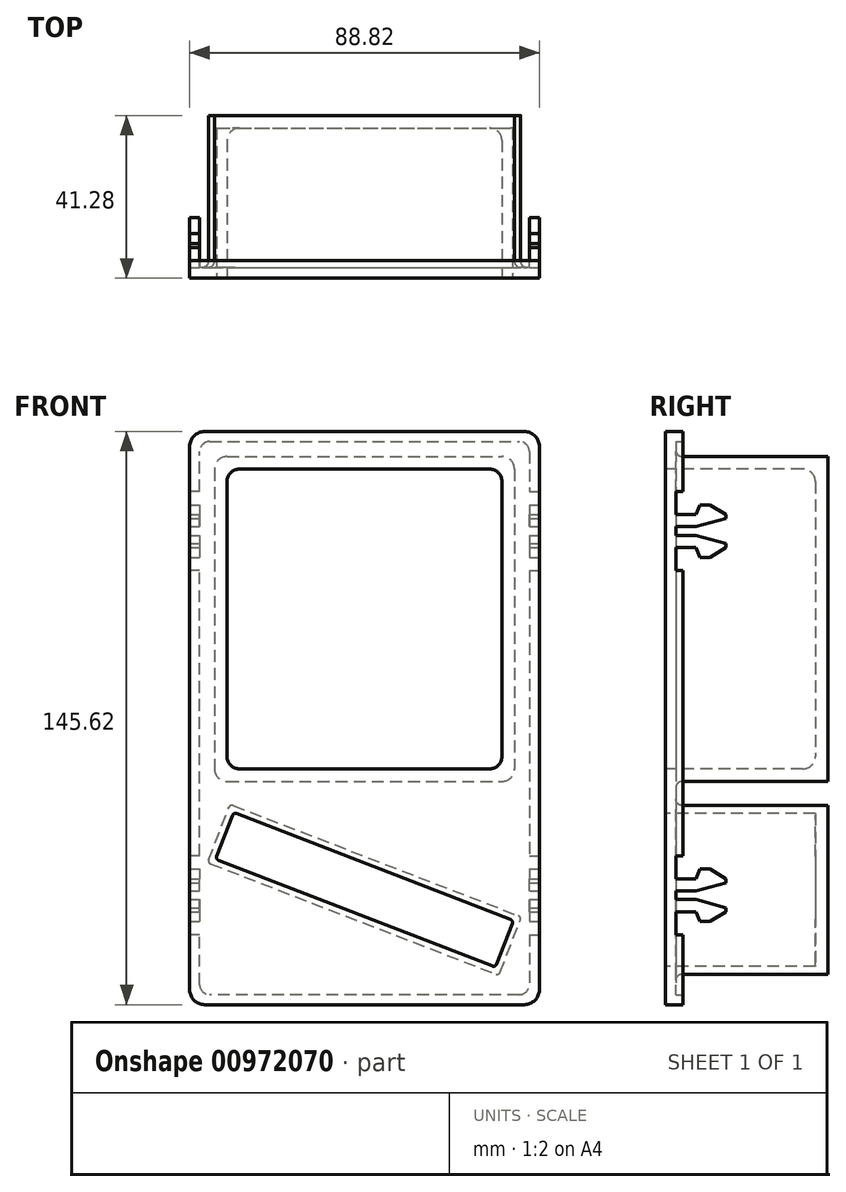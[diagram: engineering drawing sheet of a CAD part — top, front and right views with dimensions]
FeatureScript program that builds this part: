
annotation { "Feature Type Name" : "Feature", "Feature Type Description" : "" }
export const myFeature = defineFeature(function(context is Context, id is Id, definition is map)
    precondition{}
    {
        {
            var Q0;
            Q0=qCreatedBy(makeId("Front.planeOp"),FACE);
            var sketch = newSketch(context, id + "F0", { "sketchPlane" : qUnion([Q0])});
            skLineSegment(sketch, "E0.bottom", {"start": v(-40.6, 72.8) * mm, "end": v(40.6, 72.8) * mm});
            skLineSegment(sketch, "E0.top", {"start": v(-40.6, -72.8) * mm, "end": v(40.6, -72.8) * mm});
            skLineSegment(sketch, "E0.left", {"start": v(-44.41, 69) * mm, "end": v(-44.41, -69) * mm});
            skLineSegment(sketch, "E0.right", {"start": v(44.41, 69) * mm, "end": v(44.41, -69) * mm});
            skPoint(sketch, "E0.middle", {"position": v(0, 0) * mm});
            skPoint(sketch, "E1.visualSharp", {"position": v(-44.41, -72.8) * mm});
            skArc(sketch, "E1.filletArc", {"start": v(-44.41, -69) * mm, "mid": v(-43.3, -71.7) * mm, "end": v(-40.6, -72.8) * mm});
            skPoint(sketch, "E2.visualSharp", {"position": v(44.41, -72.8) * mm});
            skArc(sketch, "E2.filletArc", {"start": v(40.6, -72.8) * mm, "mid": v(43.3, -71.7) * mm, "end": v(44.41, -69) * mm});
            skPoint(sketch, "E3.visualSharp", {"position": v(44.41, 72.8) * mm});
            skArc(sketch, "E3.filletArc", {"start": v(44.41, 69) * mm, "mid": v(43.3, 71.7) * mm, "end": v(40.6, 72.8) * mm});
            skPoint(sketch, "E4.visualSharp", {"position": v(-44.41, 72.8) * mm});
            skArc(sketch, "E4.filletArc", {"start": v(-40.6, 72.8) * mm, "mid": v(-43.3, 71.7) * mm, "end": v(-44.41, 69) * mm});
            skSolve(sketch);
        }
        {
            var Q0;
            Q0=makeQuery(id+"F0.imprint","IMPRINT",FACE,{"disambiguationData":[TD([[makeQuery(id+"F0.imprint","IMPRINT",EDGE,{"derivedFrom":sQuery(id+"F0.wireOp",EDGE,"E0.bottom")}),-1.0]])]});
            extrude(context, id + "F1", {"entities" : qUnion([Q0]), "depth" : 4.44 * mm, "offsetDistance" : 25.4 * mm});
        }
        {
            var Q0;
            Q0=makeQuery(id+"F0.imprint","IMPRINT",FACE,{"disambiguationData":[TD([[makeQuery(id+"F0.imprint","IMPRINT",EDGE,{"derivedFrom":sQuery(id+"F0.wireOp",EDGE,"E0.bottom")}),-1.0]])]});
            var sketch = newSketch(context, id + "F2", { "sketchPlane" : qUnion([Q0])});
            skLineSegment(sketch, "E5", {"start": v(41.87, 67.73) * mm, "end": v(41.87, -67.73) * mm});
            skLineSegment(sketch, "E6", {"start": v(39.33, -70.27) * mm, "end": v(-39.33, -70.27) * mm});
            skLineSegment(sketch, "E7", {"start": v(-41.87, -67.73) * mm, "end": v(-41.87, 67.73) * mm});
            skLineSegment(sketch, "E8", {"start": v(-39.33, 70.27) * mm, "end": v(39.33, 70.27) * mm});
            skPoint(sketch, "E9.visualSharp", {"position": v(41.87, 70.27) * mm});
            skArc(sketch, "E9.filletArc", {"start": v(41.87, 67.73) * mm, "mid": v(41.13, 69.53) * mm, "end": v(39.33, 70.27) * mm});
            skPoint(sketch, "E10.visualSharp", {"position": v(-41.87, 70.27) * mm});
            skArc(sketch, "E10.filletArc", {"start": v(-39.33, 70.27) * mm, "mid": v(-41.13, 69.53) * mm, "end": v(-41.87, 67.73) * mm});
            skPoint(sketch, "E11.visualSharp", {"position": v(-41.87, -70.27) * mm});
            skArc(sketch, "E11.filletArc", {"start": v(-41.87, -67.73) * mm, "mid": v(-41.13, -69.53) * mm, "end": v(-39.33, -70.27) * mm});
            skPoint(sketch, "E12.visualSharp", {"position": v(41.87, -70.27) * mm});
            skArc(sketch, "E12.filletArc", {"start": v(39.33, -70.27) * mm, "mid": v(41.13, -69.53) * mm, "end": v(41.87, -67.73) * mm});
            skSolve(sketch);
        }
        {
            var Q0;
            Q0=qSketchRegion(id+"F2",true);
            extrude(context, id + "F3", {"entities" : qUnion([Q0]), "operationType" : NewBodyOperationType.REMOVE, "depth" : 1.78 * mm, "offsetDistance" : 25.4 * mm});
        }
        {
            var Q0;
            Q0=makeQuery(id+"F1.opExtrude","CAP_FACE",FACE,{"disambiguationData":[OSD([sQuery(id+"F0.wireOp",EDGE,"E0.bottom"),sQuery(id+"F0.wireOp",EDGE,"E0.top"),sQuery(id+"F0.wireOp",EDGE,"E0.left"),sQuery(id+"F0.wireOp",EDGE,"E0.right"),sQuery(id+"F0.wireOp",EDGE,"E1.filletArc"),sQuery(id+"F0.wireOp",EDGE,"E2.filletArc"),sQuery(id+"F0.wireOp",EDGE,"E3.filletArc"),sQuery(id+"F0.wireOp",EDGE,"E4.filletArc")])],"isStart":false});
            var sketch = newSketch(context, id + "F4", { "sketchPlane" : qUnion([Q0])});
            skLineSegment(sketch, "E13", {"start": v(-31.75, 63.28) * mm, "end": v(31.75, 63.28) * mm});
            skLineSegment(sketch, "E14", {"start": v(-34.93, 60.1) * mm, "end": v(-34.93, -9.74) * mm});
            skLineSegment(sketch, "E15", {"start": v(-31.75, -12.92) * mm, "end": v(31.75, -12.92) * mm});
            skLineSegment(sketch, "E16", {"start": v(34.93, -9.74) * mm, "end": v(34.93, 60.1) * mm});
            skPoint(sketch, "E17.visualSharp", {"position": v(-34.93, 63.28) * mm});
            skArc(sketch, "E17.filletArc", {"start": v(-31.75, 63.28) * mm, "mid": v(-34, 62.35) * mm, "end": v(-34.92, 60.1) * mm});
            skPoint(sketch, "E18.visualSharp", {"position": v(34.93, 63.28) * mm});
            skArc(sketch, "E18.filletArc", {"start": v(34.93, 60.1) * mm, "mid": v(34, 62.35) * mm, "end": v(31.75, 63.28) * mm});
            skPoint(sketch, "E19.visualSharp", {"position": v(-34.93, -12.92) * mm});
            skArc(sketch, "E19.filletArc", {"start": v(-34.93, -9.74) * mm, "mid": v(-34, -11.99) * mm, "end": v(-31.75, -12.92) * mm});
            skPoint(sketch, "E20.visualSharp", {"position": v(34.93, -12.92) * mm});
            skArc(sketch, "E20.filletArc", {"start": v(31.75, -12.92) * mm, "mid": v(34, -11.99) * mm, "end": v(34.93, -9.74) * mm});
            skSolve(sketch);
        }
        {
            var Q0;
            Q0=makeQuery(id+"F1.opExtrude","CAP_FACE",FACE,{"disambiguationData":[OSD([sQuery(id+"F0.wireOp",EDGE,"E0.bottom"),sQuery(id+"F0.wireOp",EDGE,"E0.top"),sQuery(id+"F0.wireOp",EDGE,"E0.left"),sQuery(id+"F0.wireOp",EDGE,"E0.right"),sQuery(id+"F0.wireOp",EDGE,"E1.filletArc"),sQuery(id+"F0.wireOp",EDGE,"E2.filletArc"),sQuery(id+"F0.wireOp",EDGE,"E3.filletArc"),sQuery(id+"F0.wireOp",EDGE,"E4.filletArc")])],"isStart":false});
            var sketch = newSketch(context, id + "F5", { "sketchPlane" : qUnion([Q0])});
            skLineSegment(sketch, "E21", {"start": v(-34.92, 66.46) * mm, "end": v(34.92, 66.46) * mm});
            skLineSegment(sketch, "E22", {"start": v(-38.1, 63.28) * mm, "end": v(-38.1, -12.92) * mm});
            skLineSegment(sketch, "E23", {"start": v(-34.92, -16.1) * mm, "end": v(34.93, -16.1) * mm});
            skLineSegment(sketch, "E24", {"start": v(38.1, 63.28) * mm, "end": v(38.1, -12.92) * mm});
            skPoint(sketch, "E25.visualSharp", {"position": v(-38.1, 66.46) * mm});
            skArc(sketch, "E25.filletArc", {"start": v(-34.92, 66.46) * mm, "mid": v(-37.17, 65.53) * mm, "end": v(-38.1, 63.28) * mm});
            skPoint(sketch, "E26.visualSharp", {"position": v(-38.1, -16.1) * mm});
            skArc(sketch, "E26.filletArc", {"start": v(-38.1, -12.92) * mm, "mid": v(-37.17, -15.16) * mm, "end": v(-34.92, -16.1) * mm});
            skPoint(sketch, "E27.visualSharp", {"position": v(38.1, -16.1) * mm});
            skArc(sketch, "E27.filletArc", {"start": v(34.93, -16.1) * mm, "mid": v(37.17, -15.16) * mm, "end": v(38.1, -12.92) * mm});
            skPoint(sketch, "E28.visualSharp", {"position": v(38.1, 66.46) * mm});
            skArc(sketch, "E28.filletArc", {"start": v(38.1, 63.28) * mm, "mid": v(37.17, 65.53) * mm, "end": v(34.92, 66.46) * mm});
            skSolve(sketch);
        }
        {
            var Q0;
            Q0=qSketchRegion(id+"F5",true);
            extrude(context, id + "F6", {"entities" : qUnion([Q0]), "operationType" : NewBodyOperationType.ADD, "oppositeDirection" : true, "depth" : 41.27 * mm, "offsetDistance" : 25.4 * mm});
        }
        {
            var Q0;
            Q0=qSketchRegion(id+"F4",true);
            extrude(context, id + "F7", {"entities" : qUnion([Q0]), "operationType" : NewBodyOperationType.REMOVE, "oppositeDirection" : true, "depth" : 38.1 * mm, "offsetDistance" : 25.4 * mm});
        }
        {
            var Q0;
            Q0=makeQuery(id+"F1.opExtrude","CAP_FACE",FACE,{"disambiguationData":[OSD([sQuery(id+"F0.wireOp",EDGE,"E0.bottom"),sQuery(id+"F0.wireOp",EDGE,"E0.top"),sQuery(id+"F0.wireOp",EDGE,"E0.left"),sQuery(id+"F0.wireOp",EDGE,"E0.right"),sQuery(id+"F0.wireOp",EDGE,"E1.filletArc"),sQuery(id+"F0.wireOp",EDGE,"E2.filletArc"),sQuery(id+"F0.wireOp",EDGE,"E3.filletArc"),sQuery(id+"F0.wireOp",EDGE,"E4.filletArc")])],"isStart":false});
            var sketch = newSketch(context, id + "F8", { "sketchPlane" : qUnion([Q0])});
            skLineSegment(sketch, "E29", {"start": v(-37.55, -35.09) * mm, "end": v(-33.83, -25.46) * mm});
            skLineSegment(sketch, "E30", {"start": v(33.53, -62.54) * mm, "end": v(37.54, -52.18) * mm});
            skLineSegment(sketch, "E31", {"start": v(-31.78, -24.55) * mm, "end": v(37.08, -51.15) * mm});
            skPoint(sketch, "E32.visualSharp", {"position": v(-33.26, -23.98) * mm});
            skLineSegment(sketch, "E33", {"start": v(-34.27, -26.6) * mm, "end": v(-33.54, -24.72) * mm});
            skLineSegment(sketch, "E34", {"start": v(-30.7, -24.97) * mm, "end": v(-32.52, -24.27) * mm});
            skLineSegment(sketch, "E35", {"start": v(-37.1, -36.11) * mm, "end": v(32.5, -63) * mm});
            skLineSegment(sketch, "E36", {"start": v(-39.15, -37.02) * mm, "end": v(33.42, -65.05) * mm});
            skLineSegment(sketch, "E37", {"start": v(-39.6, -36) * mm, "end": v(-34.45, -22.67) * mm});
            skLineSegment(sketch, "E38", {"start": v(34.44, -64.6) * mm, "end": v(39.6, -51.27) * mm});
            skLineSegment(sketch, "E39", {"start": v(-33.43, -22.21) * mm, "end": v(39.14, -50.24) * mm});
            skPoint(sketch, "E40.visualSharp", {"position": v(-34.17, -21.93) * mm});
            skArc(sketch, "E40.filletArc", {"start": v(-33.43, -22.21) * mm, "mid": v(-34.03, -22.23) * mm, "end": v(-34.45, -22.67) * mm});
            skPoint(sketch, "E41.visualSharp", {"position": v(39.88, -50.53) * mm});
            skArc(sketch, "E41.filletArc", {"start": v(39.6, -51.27) * mm, "mid": v(39.58, -50.66) * mm, "end": v(39.14, -50.24) * mm});
            skPoint(sketch, "E42.visualSharp", {"position": v(-39.89, -36.74) * mm});
            skArc(sketch, "E42.filletArc", {"start": v(-39.6, -36) * mm, "mid": v(-39.59, -36.6) * mm, "end": v(-39.15, -37.02) * mm});
            skPoint(sketch, "E43.visualSharp", {"position": v(34.16, -65.34) * mm});
            skArc(sketch, "E43.filletArc", {"start": v(33.42, -65.05) * mm, "mid": v(34.02, -65.04) * mm, "end": v(34.44, -64.6) * mm});
            skPoint(sketch, "E44.visualSharp", {"position": v(-37.83, -35.83) * mm});
            skArc(sketch, "E44.filletArc", {"start": v(-37.55, -35.09) * mm, "mid": v(-37.53, -35.7) * mm, "end": v(-37.1, -36.11) * mm});
            skArc(sketch, "E45.filletArc", {"start": v(-32.52, -24.27) * mm, "mid": v(-33.12, -24.28) * mm, "end": v(-33.54, -24.72) * mm});
            skPoint(sketch, "E46.visualSharp", {"position": v(37.82, -51.44) * mm});
            skArc(sketch, "E46.filletArc", {"start": v(37.54, -52.18) * mm, "mid": v(37.52, -51.57) * mm, "end": v(37.08, -51.15) * mm});
            skPoint(sketch, "E47.visualSharp", {"position": v(33.25, -63.28) * mm});
            skArc(sketch, "E47.filletArc", {"start": v(32.5, -63) * mm, "mid": v(33.12, -62.98) * mm, "end": v(33.53, -62.54) * mm});
            skSolve(sketch);
        }
        {
            var Q0;
            Q0=qSketchRegion(id+"F8",true);
            extrude(context, id + "F9", {"entities" : qUnion([Q0]), "operationType" : NewBodyOperationType.ADD, "oppositeDirection" : true, "depth" : 41.27 * mm, "offsetDistance" : 25.4 * mm});
        }
        {
            var Q0;
            {var subQ1=sQuery(id+"F8.wireOp",EDGE,"E29");Q0=makeQuery(id+"F8.imprint","IMPRINT",FACE,{"disambiguationData":[TD([[makeQuery(id+"F8.imprint","IMPRINT",EDGE,{"derivedFrom":subQ1}),-1.0]])]});}
            extrude(context, id + "F10", {"entities" : qUnion([Q0]), "operationType" : NewBodyOperationType.ADD, "oppositeDirection" : true, "depth" : 41.27 * mm, "offsetDistance" : 25.4 * mm, "hasSecondDirection" : true, "secondDirectionOppositeDirection" : true, "secondDirectionDepth" : 38.1 * mm});
        }
        {
            var Q0;
            Q0=makeQuery(id+"F1.opExtrude","SWEPT_FACE",FACE,{"disambiguationData":[OSD([sQuery(id+"F0.wireOp",EDGE,"E0.right")])]});
            var sketch = newSketch(context, id + "F11", { "sketchPlane" : qUnion([Q0])});
            skLineSegment(sketch, "E48", {"start": v(0, -55.03) * mm, "end": v(-1.78, -55.03) * mm});
            skLineSegment(sketch, "E49", {"start": v(-1.78, -55.03) * mm, "end": v(-1.78, -34.96) * mm});
            skLineSegment(sketch, "E50", {"start": v(-1.78, -34.96) * mm, "end": v(0, -34.96) * mm});
            skLineSegment(sketch, "E51", {"start": v(0, -34.96) * mm, "end": v(0, -55.03) * mm});
            skSolve(sketch);
        }
        {
            var Q0;
            Q0=qSketchRegion(id+"F11",true);
            extrude(context, id + "F12", {"entities" : qUnion([Q0]), "operationType" : NewBodyOperationType.REMOVE, "oppositeDirection" : true, "depth" : 2.54 * mm, "offsetDistance" : 25.4 * mm});
        }
        {
            var Q0;
            Q0=makeQuery(id+"F1.opExtrude","SWEPT_FACE",FACE,{"disambiguationData":[OSD([sQuery(id+"F0.wireOp",EDGE,"E0.left")])]});
            var sketch = newSketch(context, id + "F13", { "sketchPlane" : qUnion([Q0])});
            skLineSegment(sketch, "E52", {"start": v(0, -55.03) * mm, "end": v(1.78, -55.03) * mm});
            skLineSegment(sketch, "E53", {"start": v(1.78, -55.03) * mm, "end": v(1.78, -34.96) * mm});
            skLineSegment(sketch, "E54", {"start": v(1.78, -34.96) * mm, "end": v(0, -34.96) * mm});
            skLineSegment(sketch, "E55", {"start": v(0, -34.96) * mm, "end": v(0, -55.03) * mm});
            skSolve(sketch);
        }
        {
            var Q0;
            Q0=makeQuery(id+"F13.imprint","IMPRINT",FACE,{"disambiguationData":[TD([[makeQuery(id+"F13.imprint","IMPRINT",EDGE,{"derivedFrom":sQuery(id+"F13.wireOp",EDGE,"E52")}),1.0]])]});
            extrude(context, id + "F14", {"entities" : qUnion([Q0]), "operationType" : NewBodyOperationType.REMOVE, "oppositeDirection" : true, "depth" : 2.54 * mm, "offsetDistance" : 25.4 * mm});
        }
        {
            var Q0;
            Q0=makeQuery(id+"F1.opExtrude","SWEPT_FACE",FACE,{"disambiguationData":[OSD([sQuery(id+"F0.wireOp",EDGE,"E0.right")])]});
            var sketch = newSketch(context, id + "F15", { "sketchPlane" : qUnion([Q0])});
            skLineSegment(sketch, "E56", {"start": v(0, 57.57) * mm, "end": v(-1.78, 57.57) * mm});
            skLineSegment(sketch, "E57", {"start": v(-1.78, 57.57) * mm, "end": v(-1.78, 37.5) * mm});
            skLineSegment(sketch, "E58", {"start": v(-1.78, 37.5) * mm, "end": v(0, 37.5) * mm});
            skLineSegment(sketch, "E59", {"start": v(0, 37.5) * mm, "end": v(0, 57.57) * mm});
            skSolve(sketch);
        }
        {
            var Q0;
            Q0=qSketchRegion(id+"F15",true);
            extrude(context, id + "F16", {"entities" : qUnion([Q0]), "operationType" : NewBodyOperationType.REMOVE, "oppositeDirection" : true, "depth" : 2.54 * mm, "offsetDistance" : 25.4 * mm});
        }
        {
            var Q0;
            Q0=makeQuery(id+"F1.opExtrude","SWEPT_FACE",FACE,{"disambiguationData":[OSD([sQuery(id+"F0.wireOp",EDGE,"E0.left")])]});
            var sketch = newSketch(context, id + "F17", { "sketchPlane" : qUnion([Q0])});
            skLineSegment(sketch, "E60", {"start": v(0, 57.57) * mm, "end": v(1.78, 57.57) * mm});
            skLineSegment(sketch, "E61", {"start": v(1.78, 57.57) * mm, "end": v(1.78, 37.5) * mm});
            skLineSegment(sketch, "E62", {"start": v(1.78, 37.5) * mm, "end": v(0, 37.5) * mm});
            skLineSegment(sketch, "E63", {"start": v(0, 37.5) * mm, "end": v(0, 57.57) * mm});
            skSolve(sketch);
        }
        {
            var Q0;
            Q0=qSketchRegion(id+"F17",true);
            extrude(context, id + "F18", {"entities" : qUnion([Q0]), "operationType" : NewBodyOperationType.REMOVE, "oppositeDirection" : true, "depth" : 2.54 * mm, "offsetDistance" : 25.4 * mm});
        }
        {
            var Q0;
            Q0=makeQuery(id+"F1.opExtrude","SWEPT_FACE",FACE,{"disambiguationData":[OSD([sQuery(id+"F0.wireOp",EDGE,"E0.right")])]});
            var sketch = newSketch(context, id + "F19", { "sketchPlane" : qUnion([Q0])});
            skLineSegment(sketch, "E64", {"start": v(-1.78, -49.19) * mm, "end": v(3.3, -49.19) * mm});
            skLineSegment(sketch, "E65", {"start": v(-1.78, -46.11) * mm, "end": v(3.32, -46.11) * mm});
            skLineSegment(sketch, "E66", {"start": v(-1.78, -49.19) * mm, "end": v(-1.78, -46.11) * mm});
            skLineSegment(sketch, "E67", {"start": v(-1.78, -43.88) * mm, "end": v(-1.78, -40.8) * mm});
            skLineSegment(sketch, "E68", {"start": v(3.3, -49.19) * mm, "end": v(4.32, -51.66) * mm});
            skLineSegment(sketch, "E69", {"start": v(4.32, -51.66) * mm, "end": v(6.86, -51.66) * mm});
            skLineSegment(sketch, "E70", {"start": v(3.32, -46.11) * mm, "end": v(10.92, -48.17) * mm});
            skLineSegment(sketch, "E71", {"start": v(10.92, -48.17) * mm, "end": v(10.92, -49.19) * mm});
            skLineSegment(sketch, "E72", {"start": v(6.86, -51.66) * mm, "end": v(10.92, -49.19) * mm});
            skLineSegment(sketch, "E73.MirrorCS", {"start": v(-1.78, -43.88) * mm, "end": v(3.32, -43.88) * mm});
            skLineSegment(sketch, "E74.MirrorCS", {"start": v(3.32, -43.88) * mm, "end": v(10.92, -41.82) * mm});
            skLineSegment(sketch, "E75.MirrorCS", {"start": v(10.92, -41.82) * mm, "end": v(10.92, -40.8) * mm});
            skLineSegment(sketch, "E76.MirrorCS", {"start": v(6.86, -38.33) * mm, "end": v(10.92, -40.8) * mm});
            skLineSegment(sketch, "E77.MirrorCS", {"start": v(4.32, -38.33) * mm, "end": v(6.86, -38.33) * mm});
            skLineSegment(sketch, "E78.MirrorCS", {"start": v(3.3, -40.8) * mm, "end": v(4.32, -38.33) * mm});
            skLineSegment(sketch, "E79.MirrorCS", {"start": v(-1.78, -40.8) * mm, "end": v(3.3, -40.8) * mm});
            skLineSegment(sketch, "E80.MirrorCS", {"start": v(-1.78, -40.8) * mm, "end": v(-1.78, -43.88) * mm});
            skLineSegment(sketch, "E81.MirrorCS", {"start": v(-1.78, 43.35) * mm, "end": v(3.3, 43.35) * mm});
            skLineSegment(sketch, "E82.MirrorCS", {"start": v(-1.78, 43.35) * mm, "end": v(-1.78, 46.42) * mm});
            skLineSegment(sketch, "E83.MirrorCS", {"start": v(-1.78, 46.42) * mm, "end": v(3.32, 46.42) * mm});
            skLineSegment(sketch, "E84.MirrorCS", {"start": v(3.32, 46.42) * mm, "end": v(10.92, 44.36) * mm});
            skLineSegment(sketch, "E85.MirrorCS", {"start": v(6.86, 40.87) * mm, "end": v(10.92, 43.35) * mm});
            skLineSegment(sketch, "E86.MirrorCS", {"start": v(10.92, 44.36) * mm, "end": v(10.92, 43.35) * mm});
            skLineSegment(sketch, "E87.MirrorCS", {"start": v(4.32, 40.87) * mm, "end": v(6.86, 40.87) * mm});
            skLineSegment(sketch, "E88.MirrorCS", {"start": v(3.3, 43.35) * mm, "end": v(4.32, 40.87) * mm});
            skLineSegment(sketch, "E89.MirrorCS", {"start": v(-1.78, 51.73) * mm, "end": v(-1.78, 48.65) * mm});
            skLineSegment(sketch, "E90.MirrorCS", {"start": v(-1.78, 48.65) * mm, "end": v(3.32, 48.65) * mm});
            skLineSegment(sketch, "E91.MirrorCS", {"start": v(3.32, 48.65) * mm, "end": v(10.92, 50.71) * mm});
            skLineSegment(sketch, "E92.MirrorCS", {"start": v(10.92, 50.71) * mm, "end": v(10.92, 51.73) * mm});
            skLineSegment(sketch, "E93.MirrorCS", {"start": v(6.86, 54.2) * mm, "end": v(10.92, 51.73) * mm});
            skLineSegment(sketch, "E94.MirrorCS", {"start": v(4.32, 54.2) * mm, "end": v(6.86, 54.2) * mm});
            skLineSegment(sketch, "E95.MirrorCS", {"start": v(3.3, 51.73) * mm, "end": v(4.32, 54.2) * mm});
            skLineSegment(sketch, "E96.MirrorCS", {"start": v(-1.78, 51.73) * mm, "end": v(3.3, 51.73) * mm});
            skSolve(sketch);
        }
        {
            var Q0;
            Q0=qSketchRegion(id+"F19",true);
            extrude(context, id + "F20", {"entities" : qUnion([Q0]), "operationType" : NewBodyOperationType.ADD, "oppositeDirection" : true, "depth" : 2.54 * mm, "offsetDistance" : 25.4 * mm, "hasSecondDirection" : true, "secondDirectionOppositeDirection" : true, "secondDirectionDepth" : 0 * mm});
        }
        {
            var Q0;
            Q0=qSketchRegion(id+"F19",true);
            extrude(context, id + "F21", {"entities" : qUnion([Q0]), "operationType" : NewBodyOperationType.ADD, "oppositeDirection" : true, "depth" : 88.82 * mm, "offsetDistance" : 25.4 * mm, "hasSecondDirection" : true, "secondDirectionOppositeDirection" : true, "secondDirectionDepth" : 86.28 * mm});
        }
        {
            var Q0;
            {var subQ1=sQuery(id+"F8.wireOp",EDGE,"E29");Q0=makeQuery(id+"F8.imprint","IMPRINT",FACE,{"disambiguationData":[TD([[makeQuery(id+"F8.imprint","IMPRINT",EDGE,{"derivedFrom":subQ1}),-1.0]])]});}
            extrude(context, id + "F22", {"entities" : qUnion([Q0]), "operationType" : NewBodyOperationType.REMOVE, "oppositeDirection" : true, "depth" : 12.7 * mm, "offsetDistance" : 25.4 * mm});
        }
        {
            var Q0;
            Q0=makeQuery(id+"F10.opExtrude","CAP_EDGE",EDGE,{"disambiguationData":[OSD([sQuery(id+"F8.wireOp",EDGE,"E29"),sQuery(id+"F8.wireOp",EDGE,"E33")])],"isStart":true});
            var Q1;
            Q1=makeQuery(id+"F9.boolean.opBoolean","INTERSECT",EDGE,{"derivedFrom":[makeQuery(id+"F3.boolean.opBoolean","COPY",FACE,{"derivedFrom":makeQuery(id+"F3.opExtrude","CAP_FACE",FACE,{"disambiguationData":[OSD([sQuery(id+"F2.wireOp",EDGE,"E5"),sQuery(id+"F2.wireOp",EDGE,"E6"),sQuery(id+"F2.wireOp",EDGE,"E7"),sQuery(id+"F2.wireOp",EDGE,"E8"),sQuery(id+"F2.wireOp",EDGE,"E9.filletArc"),sQuery(id+"F2.wireOp",EDGE,"E10.filletArc"),sQuery(id+"F2.wireOp",EDGE,"E11.filletArc"),sQuery(id+"F2.wireOp",EDGE,"E12.filletArc")])],"isStart":false})}),makeQuery(id+"F9.opExtrude","SWEPT_FACE",FACE,{"disambiguationData":[OSD([sQuery(id+"F8.wireOp",EDGE,"E36")])]})]});
            var Q2;
            Q2=makeQuery(id+"F6.boolean.opBoolean","INTERSECT",EDGE,{"derivedFrom":[makeQuery(id+"F3.boolean.opBoolean","COPY",FACE,{"derivedFrom":makeQuery(id+"F3.opExtrude","CAP_FACE",FACE,{"disambiguationData":[OSD([sQuery(id+"F2.wireOp",EDGE,"E5"),sQuery(id+"F2.wireOp",EDGE,"E6"),sQuery(id+"F2.wireOp",EDGE,"E7"),sQuery(id+"F2.wireOp",EDGE,"E8"),sQuery(id+"F2.wireOp",EDGE,"E9.filletArc"),sQuery(id+"F2.wireOp",EDGE,"E10.filletArc"),sQuery(id+"F2.wireOp",EDGE,"E11.filletArc"),sQuery(id+"F2.wireOp",EDGE,"E12.filletArc")])],"isStart":false})}),makeQuery(id+"F6.opExtrude","SWEPT_FACE",FACE,{"disambiguationData":[OSD([sQuery(id+"F5.wireOp",EDGE,"E22")])]})]});
            fillet(context, id + "F23", {"entities" : qUnion([Q0, Q1, Q2]), "radius" : 1.59 * mm, "tangentPropagation" : true, "allowEdgeOverflow" : false});
        }
        {
            var Q0;
            Q0=makeQuery(id+"F7.boolean.opBoolean","COPY",EDGE,{"derivedFrom":makeQuery(id+"F7.opExtrude","CAP_EDGE",EDGE,{"disambiguationData":[OSD([sQuery(id+"F4.wireOp",EDGE,"E15")])],"isStart":false})});
            fillet(context, id + "F24", {"entities" : qUnion([Q0]), "radius" : 3.17 * mm, "tangentPropagation" : true, "allowEdgeOverflow" : false});
        }
    });
